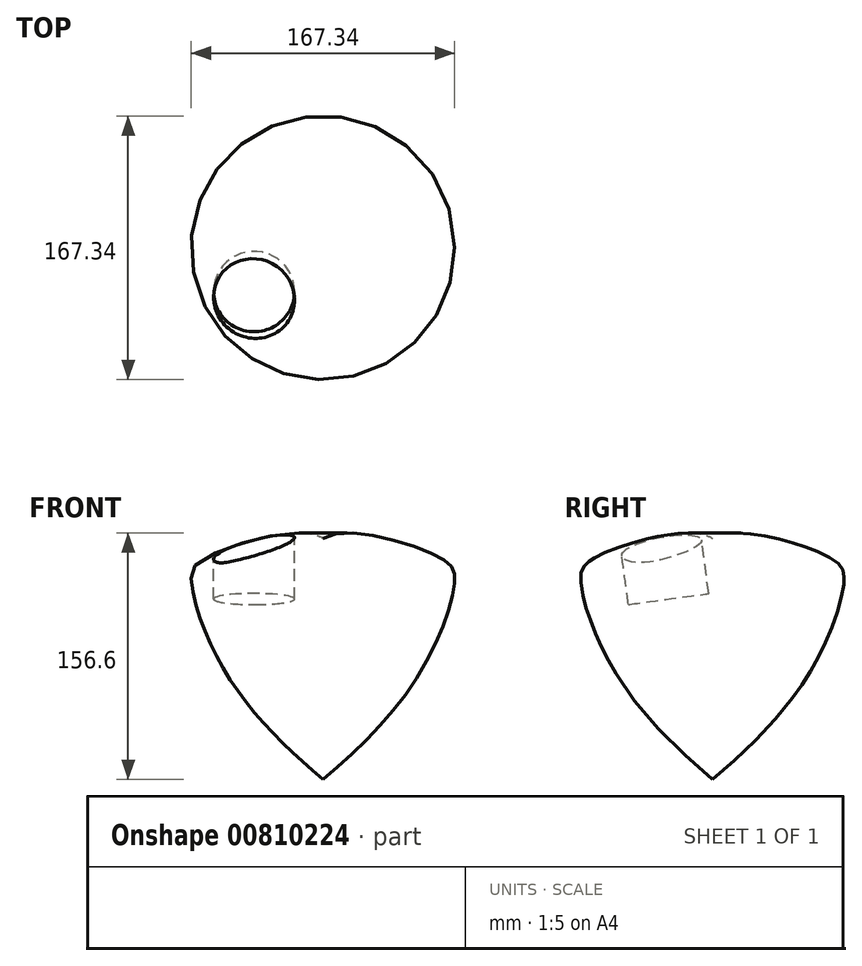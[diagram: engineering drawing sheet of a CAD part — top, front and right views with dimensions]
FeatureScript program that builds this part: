
annotation { "Feature Type Name" : "Feature", "Feature Type Description" : "" }
export const myFeature = defineFeature(function(context is Context, id is Id, definition is map)
    precondition{}
    {
        {
            var Q0;
            Q0=qCreatedBy(makeId("Front.planeOp"),FACE);
            var sketch = newSketch(context, id + "F0", { "sketchPlane" : qUnion([Q0])});
            skLineSegment(sketch, "E0", {"start": v(0, 108.07) * mm, "end": v(0, -105.82) * mm, "construction": true});
            skLineSegment(sketch, "E1", {"start": v(0, -105.82) * mm, "end": v(0, 8.85) * mm});
            skFitSpline(sketch, "E2", {"points": [v(0, 79.97) * mm, v(73.78, 68.16) * mm, v(83.62, 52.98) * mm, v(60.57, -7.17) * mm, v(0, -73.22) * mm], "startDerivative": vector(138.08, 99.6) * mm, "endDerivative": vector(-214.65, -181.03) * mm});
            skLineSegment(sketch, "E3", {"start": v(0, 79.97) * mm, "end": v(0, -73.22) * mm});
            skSolve(sketch);
        }
        {
            var Q0;
            Q0 = qSketchRegion(id + "F0", true);
            var Q1;
            Q1=sQuery(id+"F0.wireOp",EDGE,"E0");
            revolve(context, id + "F1", {"surfaceOperationType" : NewSurfaceOperationType.NEW, "entities" : qUnion([Q0]), "axis" : qUnion([Q1]), "revolveType" : RevolveType.FULL});
        }
        {
            var Q0;
            Q0=qCreatedBy(makeId("Top.planeOp"),FACE);
            cPlane(context, id + "F2", {"entities" : qUnion([Q0]), "cplaneType" : CPlaneType.OFFSET, "offset" : 119.9 * mm, "width" : 150 * mm, "height" : 150 * mm});
        }
        {
            var Q0;
            Q0=qCreatedBy(id+"F2.planeOp",FACE);
            var sketch = newSketch(context, id + "F3", { "sketchPlane" : qUnion([Q0])});
            skLineSegment(sketch, "E4", {"start": v(-113.72, 0) * mm, "end": v(121.36, 0) * mm});
            skSolve(sketch);
        }
        {
            var Q0;
            Q0=sQuery(id+"F3.wireOp",EDGE,"E4");
            cPlane(context, id + "F4", {"entities" : qUnion([Q0]), "cplaneType" : CPlaneType.LINE_ANGLE, "offset" : 25 * mm, "angle" : 97.78 * degree, "width" : 150 * mm, "height" : 150 * mm});
        }
        {
            var Q0;
            Q0=qCreatedBy(id+"F4.planeOp",FACE);
            var sketch = newSketch(context, id + "F5", { "sketchPlane" : qUnion([Q0])});
            skCircle(sketch, "E5", {"center": v(-43.77, -21.97) * mm, "radius": 25.74 * mm});
            skSolve(sketch);
        }
        {
            var Q0;
            Q0 = qSketchRegion(id + "F5", true);
            extrude(context, id + "F6", {"entities" : qUnion([Q0]), "operationType" : NewBodyOperationType.REMOVE, "oppositeDirection" : true, "depth" : 74 * mm, "offsetDistance" : 25 * mm});
        }
    });
